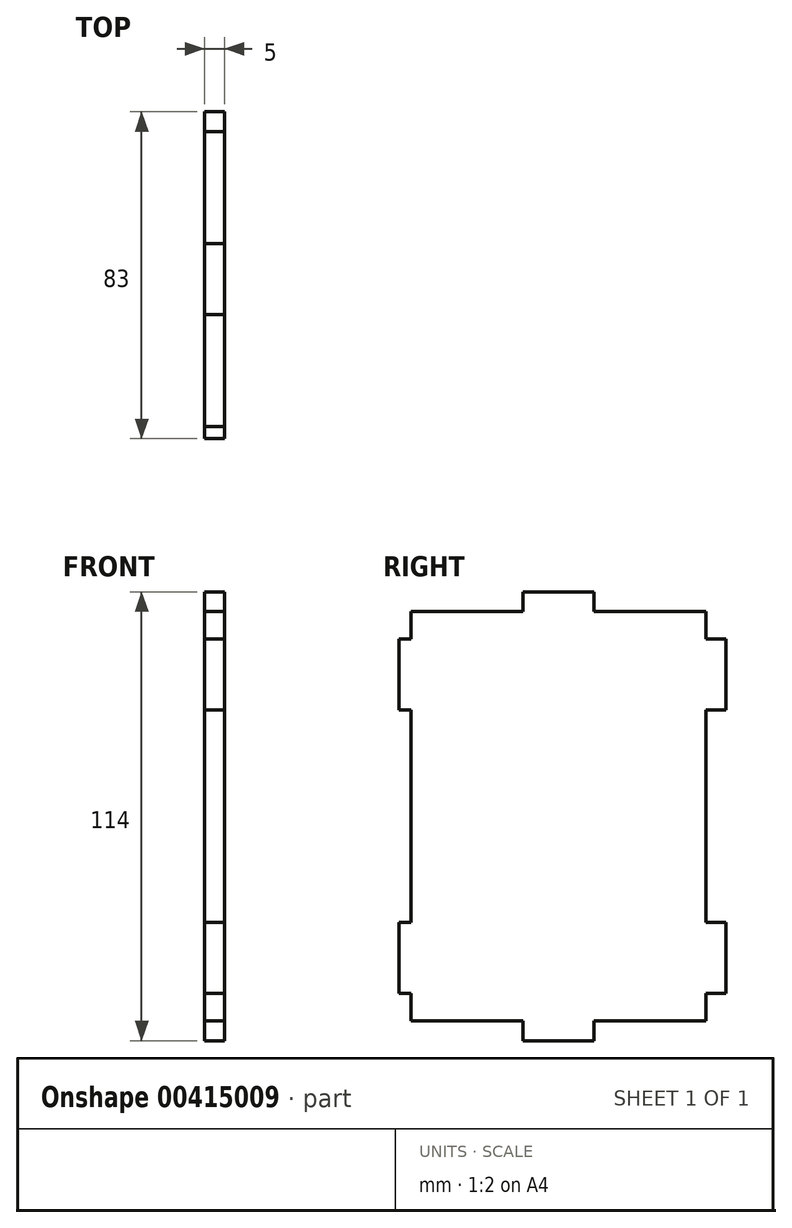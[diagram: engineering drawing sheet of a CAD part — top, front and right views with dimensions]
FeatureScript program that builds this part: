
annotation { "Feature Type Name" : "Feature", "Feature Type Description" : "" }
export const myFeature = defineFeature(function(context is Context, id is Id, definition is map)
    precondition{}
    {
        {
            var Q0;
            Q0=qCreatedBy(makeId("Right.planeOp"),FACE);
            var sketch = newSketch(context, id + "F0", { "sketchPlane" : qUnion([Q0])});
            skLineSegment(sketch, "E0.bottom", {"start": v(37.5, 52) * mm, "end": v(9, 52) * mm});
            skLineSegment(sketch, "E0.top", {"start": v(37.5, -52) * mm, "end": v(9, -52) * mm});
            skLineSegment(sketch, "E0.left", {"start": v(37.5, 52) * mm, "end": v(37.5, 45) * mm});
            skLineSegment(sketch, "E0.right", {"start": v(-37.5, 52) * mm, "end": v(-37.5, 45) * mm});
            skPoint(sketch, "E0.middle", {"position": v(0, 0) * mm});
            skLineSegment(sketch, "E1.bottom", {"start": v(37.5, 45) * mm, "end": v(42.5, 45) * mm});
            skLineSegment(sketch, "E1.top", {"start": v(37.5, 27) * mm, "end": v(42.5, 27) * mm});
            skLineSegment(sketch, "E1.right", {"start": v(42.5, 45) * mm, "end": v(42.5, 27) * mm});
            skLineSegment(sketch, "E2.bottom", {"start": v(37.5, -27) * mm, "end": v(42.5, -27) * mm});
            skLineSegment(sketch, "E2.top", {"start": v(37.5, -45) * mm, "end": v(42.5, -45) * mm});
            skLineSegment(sketch, "E2.right", {"start": v(42.5, -27) * mm, "end": v(42.5, -45) * mm});
            skLineSegment(sketch, "E3.top", {"start": v(-9, 57) * mm, "end": v(9, 57) * mm});
            skLineSegment(sketch, "E3.left", {"start": v(-9, 52) * mm, "end": v(-9, 57) * mm});
            skLineSegment(sketch, "E3.right", {"start": v(9, 52) * mm, "end": v(9, 57) * mm});
            skLineSegment(sketch, "E4.top", {"start": v(-9, -57) * mm, "end": v(9, -57) * mm});
            skLineSegment(sketch, "E4.left", {"start": v(-9, -52) * mm, "end": v(-9, -57) * mm});
            skLineSegment(sketch, "E4.right", {"start": v(9, -52) * mm, "end": v(9, -57) * mm});
            skLineSegment(sketch, "E5.trimOffspring", {"start": v(-9, 52) * mm, "end": v(-37.5, 52) * mm});
            skLineSegment(sketch, "E6.trimOffspring", {"start": v(37.5, 27) * mm, "end": v(37.5, -27) * mm});
            skLineSegment(sketch, "E7.trimOffspring", {"start": v(37.5, -45) * mm, "end": v(37.5, -52) * mm});
            skLineSegment(sketch, "E8.trimOffspring", {"start": v(-37.5, -45) * mm, "end": v(-37.5, -52) * mm});
            skLineSegment(sketch, "E9.trimOffspring", {"start": v(-9, -52) * mm, "end": v(-37.5, -52) * mm});
            skLineSegment(sketch, "E10", {"start": v(0, 0) * mm, "end": v(17.02, 0) * mm, "construction": true});
            skLineSegment(sketch, "E11", {"start": v(0, 0) * mm, "end": v(0, 15.14) * mm, "construction": true});
            skLineSegment(sketch, "E12", {"start": v(-37.5, 45) * mm, "end": v(-40.5, 45) * mm});
            skLineSegment(sketch, "E13", {"start": v(-40.5, 45) * mm, "end": v(-40.5, 27) * mm});
            skLineSegment(sketch, "E14", {"start": v(-40.5, 27) * mm, "end": v(-37.5, 27) * mm});
            skLineSegment(sketch, "E15", {"start": v(-37.5, 27) * mm, "end": v(-37.5, -27) * mm});
            skLineSegment(sketch, "E16", {"start": v(-37.5, -27) * mm, "end": v(-40.5, -27) * mm});
            skLineSegment(sketch, "E17", {"start": v(-40.5, -27) * mm, "end": v(-40.5, -45) * mm});
            skLineSegment(sketch, "E18", {"start": v(-40.5, -45) * mm, "end": v(-37.5, -45) * mm});
            skSolve(sketch);
        }
        {
            var Q0;
            Q0=makeQuery(id+"F0.imprint","IMPRINT",FACE,{"disambiguationData":[TD([[makeQuery(id+"F0.imprint","IMPRINT",EDGE,{"derivedFrom":sQuery(id+"F0.wireOp",EDGE,"E0.bottom")}),1.0]])]});
            extrude(context, id + "F1", {"entities" : qUnion([Q0]), "depth" : 5 * mm});
        }
    });
